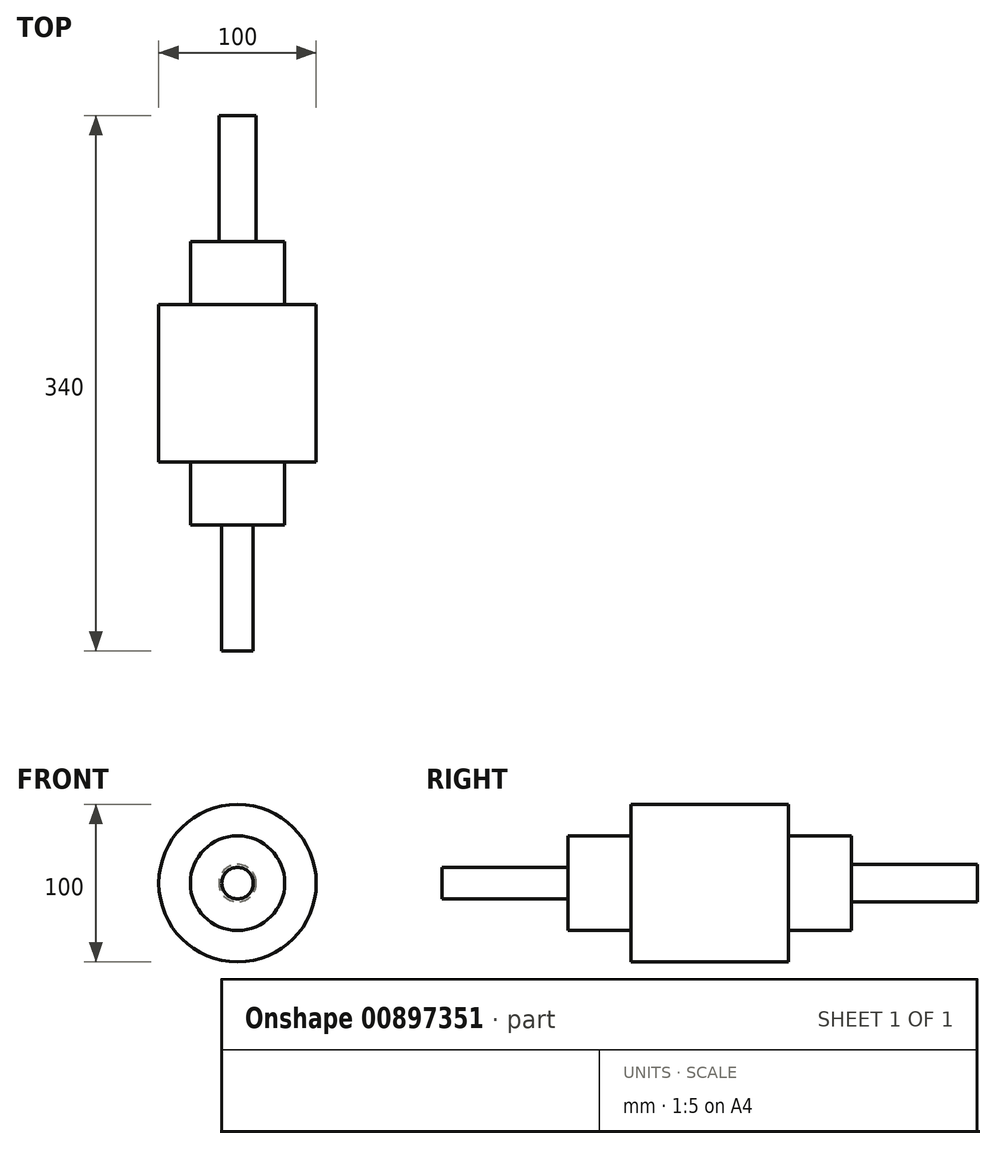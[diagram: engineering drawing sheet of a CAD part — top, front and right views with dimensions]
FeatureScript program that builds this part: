
annotation { "Feature Type Name" : "Feature", "Feature Type Description" : "" }
export const myFeature = defineFeature(function(context is Context, id is Id, definition is map)
    precondition{}
    {
        {
            var Q0;
            Q0=qCreatedBy(makeId("Front.planeOp"),FACE);
            var sketch = newSketch(context, id + "F0", { "sketchPlane" : qUnion([Q0])});
            skCircle(sketch, "E0", {"center": v(0, 0) * mm, "radius": 50 * mm});
            skSolve(sketch);
        }
        {
            var Q0;
            Q0=makeQuery(id+"F0.imprint","IMPRINT",FACE,{"disambiguationData":[TD([[makeQuery(id+"F0.imprint","IMPRINT",EDGE,{"derivedFrom":sQuery(id+"F0.wireOp",EDGE,"E0")}),1.0]])]});
            extrude(context, id + "F1", {"entities" : qUnion([Q0]), "depth" : 40 * mm, "offsetDistance" : 25.4 * mm});
        }
        {
            var Q0;
            Q0=makeQuery(id+"F1.opExtrude","CAP_FACE",FACE,{"disambiguationData":[OSD([sQuery(id+"F0.wireOp",EDGE,"E0")])],"isStart":false});
            extrude(context, id + "F2", {"entities" : qUnion([Q0]), "operationType" : NewBodyOperationType.ADD, "depth" : 60 * mm, "offsetDistance" : 25.4 * mm});
        }
        {
            var Q0;
            Q0=makeQuery(id+"F2.opExtrude","CAP_FACE",FACE,{"disambiguationData":[OSD([sQuery(id+"F0.wireOp",EDGE,"E0")])],"isStart":false});
            var sketch = newSketch(context, id + "F3", { "sketchPlane" : qUnion([Q0])});
            skCircle(sketch, "E1", {"center": v(0, 0) * mm, "radius": 30 * mm});
            skSolve(sketch);
        }
        {
            var Q0;
            Q0=makeQuery(id+"F3.imprint","IMPRINT",FACE,{"disambiguationData":[TD([[makeQuery(id+"F3.imprint","IMPRINT",EDGE,{"derivedFrom":sQuery(id+"F3.wireOp",EDGE,"E1")}),1.0]])]});
            extrude(context, id + "F4", {"entities" : qUnion([Q0]), "operationType" : NewBodyOperationType.ADD, "depth" : 40 * mm, "offsetDistance" : 25.4 * mm});
        }
        {
            var Q0;
            Q0=makeQuery(id+"F4.opExtrude","CAP_FACE",FACE,{"disambiguationData":[OSD([sQuery(id+"F3.wireOp",EDGE,"E1")])],"isStart":false});
            var sketch = newSketch(context, id + "F5", { "sketchPlane" : qUnion([Q0])});
            skCircle(sketch, "E2", {"center": v(0, 0) * mm, "radius": 10 * mm});
            skSolve(sketch);
        }
        {
            var Q0;
            Q0=makeQuery(id+"F5.imprint","IMPRINT",FACE,{"disambiguationData":[TD([[makeQuery(id+"F5.imprint","IMPRINT",EDGE,{"derivedFrom":sQuery(id+"F5.wireOp",EDGE,"E2")}),1.0]])]});
            extrude(context, id + "F6", {"entities" : qUnion([Q0]), "operationType" : NewBodyOperationType.ADD, "depth" : 80 * mm, "offsetDistance" : 25.4 * mm});
        }
        {
            var Q0;
            Q0=makeQuery(id+"F1.opExtrude","CAP_FACE",FACE,{"disambiguationData":[OSD([sQuery(id+"F0.wireOp",EDGE,"E0")])],"isStart":true});
            var sketch = newSketch(context, id + "F7", { "sketchPlane" : qUnion([Q0])});
            skCircle(sketch, "E3", {"center": v(0, 0) * mm, "radius": 30 * mm});
            skSolve(sketch);
        }
        {
            var Q0;
            Q0=makeQuery(id+"F7.imprint","IMPRINT",FACE,{"disambiguationData":[TD([[makeQuery(id+"F7.imprint","IMPRINT",EDGE,{"derivedFrom":sQuery(id+"F7.wireOp",EDGE,"E3")}),1.0]])]});
            extrude(context, id + "F8", {"entities" : qUnion([Q0]), "operationType" : NewBodyOperationType.ADD, "depth" : 40 * mm, "offsetDistance" : 25.4 * mm});
        }
        {
            var Q0;
            Q0=makeQuery(id+"F8.opExtrude","CAP_FACE",FACE,{"disambiguationData":[OSD([sQuery(id+"F7.wireOp",EDGE,"E3")])],"isStart":false});
            var sketch = newSketch(context, id + "F9", { "sketchPlane" : qUnion([Q0])});
            skCircle(sketch, "E4", {"center": v(0, 0) * mm, "radius": 11.89 * mm});
            skSolve(sketch);
        }
        {
            var Q0;
            Q0=makeQuery(id+"F9.imprint","IMPRINT",FACE,{"disambiguationData":[TD([[makeQuery(id+"F9.imprint","IMPRINT",EDGE,{"derivedFrom":sQuery(id+"F9.wireOp",EDGE,"E4")}),1.0]])]});
            extrude(context, id + "F10", {"entities" : qUnion([Q0]), "operationType" : NewBodyOperationType.ADD, "depth" : 80 * mm, "offsetDistance" : 25.4 * mm});
        }
    });
